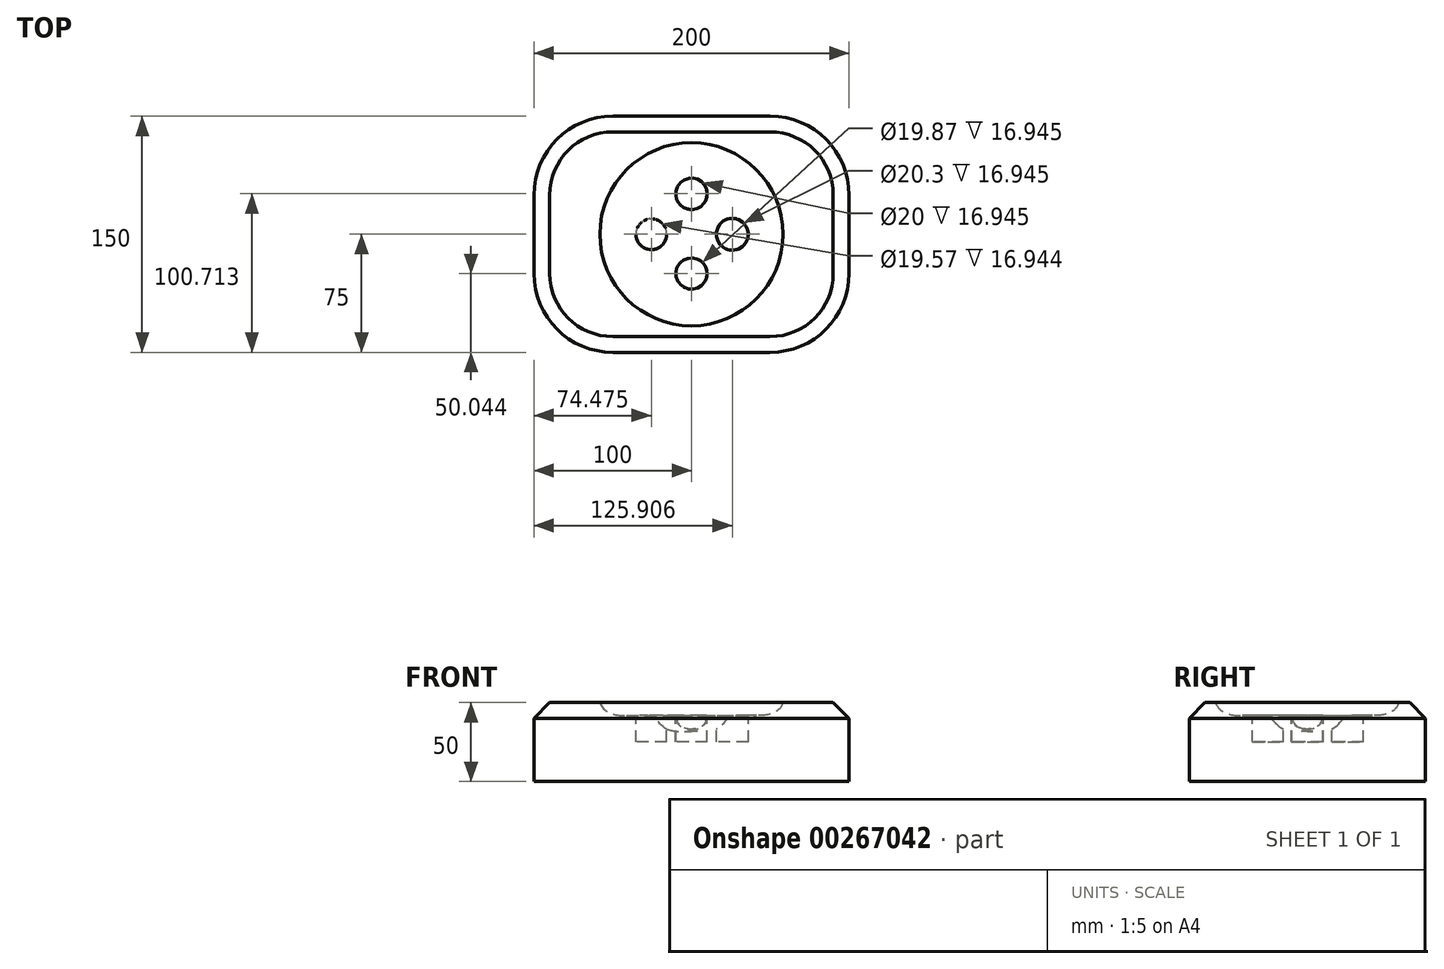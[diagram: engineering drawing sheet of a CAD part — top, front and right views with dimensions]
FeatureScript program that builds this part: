
annotation { "Feature Type Name" : "Feature", "Feature Type Description" : "" }
export const myFeature = defineFeature(function(context is Context, id is Id, definition is map)
    precondition{}
    {
        {
            var Q0;
            Q0=qCreatedBy(makeId("Top.planeOp"),FACE);
            var sketch = newSketch(context, id + "F0", { "sketchPlane" : qUnion([Q0])});
            skLineSegment(sketch, "E0.bottom", {"start": v(-100, 75) * mm, "end": v(100, 75) * mm});
            skLineSegment(sketch, "E0.top", {"start": v(-100, -75) * mm, "end": v(100, -75) * mm});
            skLineSegment(sketch, "E0.left", {"start": v(-100, 75) * mm, "end": v(-100, -75) * mm});
            skLineSegment(sketch, "E0.right", {"start": v(100, 75) * mm, "end": v(100, -75) * mm});
            skSolve(sketch);
        }
        {
            var Q0;
            Q0=makeQuery(id+"F0.imprint","IMPRINT",FACE,{"disambiguationData":[TD([[makeQuery(id+"F0.imprint","IMPRINT",EDGE,{"derivedFrom":sQuery(id+"F0.wireOp",EDGE,"E0.bottom")}),-1.0]])]});
            extrude(context, id + "F1", {"entities" : qUnion([Q0]), "endBound" : BoundingType.SYMMETRIC, "depth" : 50 * mm});
        }
        {
            var Q0;
            Q0=makeQuery(id+"F1.opExtrude","SWEPT_EDGE",EDGE,{"disambiguationData":[OSD([sQuery(id+"F0.wireOp",EDGE,"E0.top"),sQuery(id+"F0.wireOp",EDGE,"E0.left")])]});
            var Q1;
            Q1=makeQuery(id+"F1.opExtrude","SWEPT_EDGE",EDGE,{"disambiguationData":[OSD([sQuery(id+"F0.wireOp",EDGE,"E0.top"),sQuery(id+"F0.wireOp",EDGE,"E0.right")])]});
            var Q2;
            Q2=makeQuery(id+"F1.opExtrude","SWEPT_EDGE",EDGE,{"disambiguationData":[OSD([sQuery(id+"F0.wireOp",EDGE,"E0.bottom"),sQuery(id+"F0.wireOp",EDGE,"E0.right")])]});
            var Q3;
            Q3=makeQuery(id+"F1.opExtrude","SWEPT_EDGE",EDGE,{"disambiguationData":[OSD([sQuery(id+"F0.wireOp",EDGE,"E0.bottom"),sQuery(id+"F0.wireOp",EDGE,"E0.left")])]});
            fillet(context, id + "F2", {"entities" : qUnion([Q0, Q1, Q2, Q3]), "radius" : 50 * mm, "tangentPropagation" : true, "allowEdgeOverflow" : false});
        }
        {
            var Q0;
            Q0=qCreatedBy(makeId("Front.planeOp"),FACE);
            var sketch = newSketch(context, id + "F3", { "sketchPlane" : qUnion([Q0])});
            skFitSpline(sketch, "E1", {"points": [v(-58.16, 25) * mm, v(-28.1, 16.5) * mm, v(0, 6.65) * mm], "startDerivative": vector(25.2, -72.8) * mm, "endDerivative": vector(144.88, 6.44) * mm});
            skLineSegment(sketch, "E2", {"start": v(-58.16, 25) * mm, "end": v(0, 25) * mm});
            skLineSegment(sketch, "E3", {"start": v(0, 6.65) * mm, "end": v(0, 25) * mm});
            skSolve(sketch);
        }
        {
            var Q0;
            Q0 = qSketchRegion(id + "F3", true);
            var Q1;
            Q1=sQuery(id+"F3.wireOp",EDGE,"E3");
            revolve(context, id + "F4", {"operationType" : NewBodyOperationType.REMOVE, "entities" : qUnion([Q0]), "axis" : qUnion([Q1]), "revolveType" : RevolveType.FULL, "oppositeDirection" : true});
        }
        {
            var Q0;
            Q0=makeQuery(id+"F1.opExtrude","CAP_EDGE",EDGE,{"disambiguationData":[OSD([sQuery(id+"F0.wireOp",EDGE,"E0.top")])],"isStart":false});
            chamfer(context, id + "F5", {"entities" : qUnion([Q0]), "width" : 10 * mm, "tangentPropagation" : true});
        }
        {
            var Q0;
            Q0=makeQuery(id+"F1.opExtrude","CAP_FACE",FACE,{"disambiguationData":[OSD([sQuery(id+"F0.wireOp",EDGE,"E0.bottom"),sQuery(id+"F0.wireOp",EDGE,"E0.top"),sQuery(id+"F0.wireOp",EDGE,"E0.left"),sQuery(id+"F0.wireOp",EDGE,"E0.right")])],"isStart":false});
            var sketch = newSketch(context, id + "F6", { "sketchPlane" : qUnion([Q0])});
            skCircle(sketch, "E4", {"center": v(0, 25.71) * mm, "radius": 10 * mm});
            skCircle(sketch, "E5", {"center": v(25.9, 0) * mm, "radius": 10.15 * mm});
            skCircle(sketch, "E6", {"center": v(0, -24.96) * mm, "radius": 9.93 * mm});
            skCircle(sketch, "E7", {"center": v(-25.52, 0) * mm, "radius": 9.78 * mm});
            skSolve(sketch);
        }
        {
            var Q0;
            Q0=makeQuery(id+"F6.imprint","IMPRINT",FACE,{"disambiguationData":[TD([[makeQuery(id+"F6.imprint","IMPRINT",EDGE,{"derivedFrom":sQuery(id+"F6.wireOp",EDGE,"E7")}),1.0]])]});
            var Q1;
            Q1=makeQuery(id+"F6.imprint","IMPRINT",FACE,{"disambiguationData":[TD([[makeQuery(id+"F6.imprint","IMPRINT",EDGE,{"derivedFrom":sQuery(id+"F6.wireOp",EDGE,"E4")}),1.0]])]});
            var Q2;
            Q2=makeQuery(id+"F6.imprint","IMPRINT",FACE,{"disambiguationData":[TD([[makeQuery(id+"F6.imprint","IMPRINT",EDGE,{"derivedFrom":sQuery(id+"F6.wireOp",EDGE,"E5")}),1.0]])]});
            var Q3;
            Q3=makeQuery(id+"F6.imprint","IMPRINT",FACE,{"disambiguationData":[TD([[makeQuery(id+"F6.imprint","IMPRINT",EDGE,{"derivedFrom":sQuery(id+"F6.wireOp",EDGE,"E6")}),1.0]])]});
            extrude(context, id + "F7", {"entities" : qUnion([Q0, Q1, Q2, Q3]), "operationType" : NewBodyOperationType.REMOVE, "oppositeDirection" : true, "depth" : 25 * mm});
        }
    });
